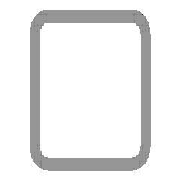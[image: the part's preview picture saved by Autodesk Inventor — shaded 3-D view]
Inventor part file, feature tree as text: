
AUTODESK INVENTOR PART (.ipt)
format: ipt  version: 2024.2 (Build 282272000, 272)  size: 128,000 bytes
history: native  units: mm (DEFAULTED — no unit token found)
features: other x4, sketch x1, plane x1
ambient origin geometry x8: Origin, YZ Plane, XZ Plane, XY Plane, X Axis, Y Axis, Z Axis, Center Point
bodies: Solid1 (feature_tree), Body (feature_tree)
feature tree (6):
  parser-record x1  (decoder bookkeeping rows leaked as tree rows — omitted from the tree; the rows remain in map.json)
  other  "Driven Length"
  other  "Start Plane"
  other  "End Plane"
  sketch  "Sketch3"  dims[d3=420.0mm d4=0.0mm d7=4.0mm d9=40.0mm d11=40.0mm d12=2.0mm d13=40.0mm d14=460.0mm d15=20.0mm d16=20.0mm d17=90.0deg d18=420.0mm]
  plane  "Work Plane3"
